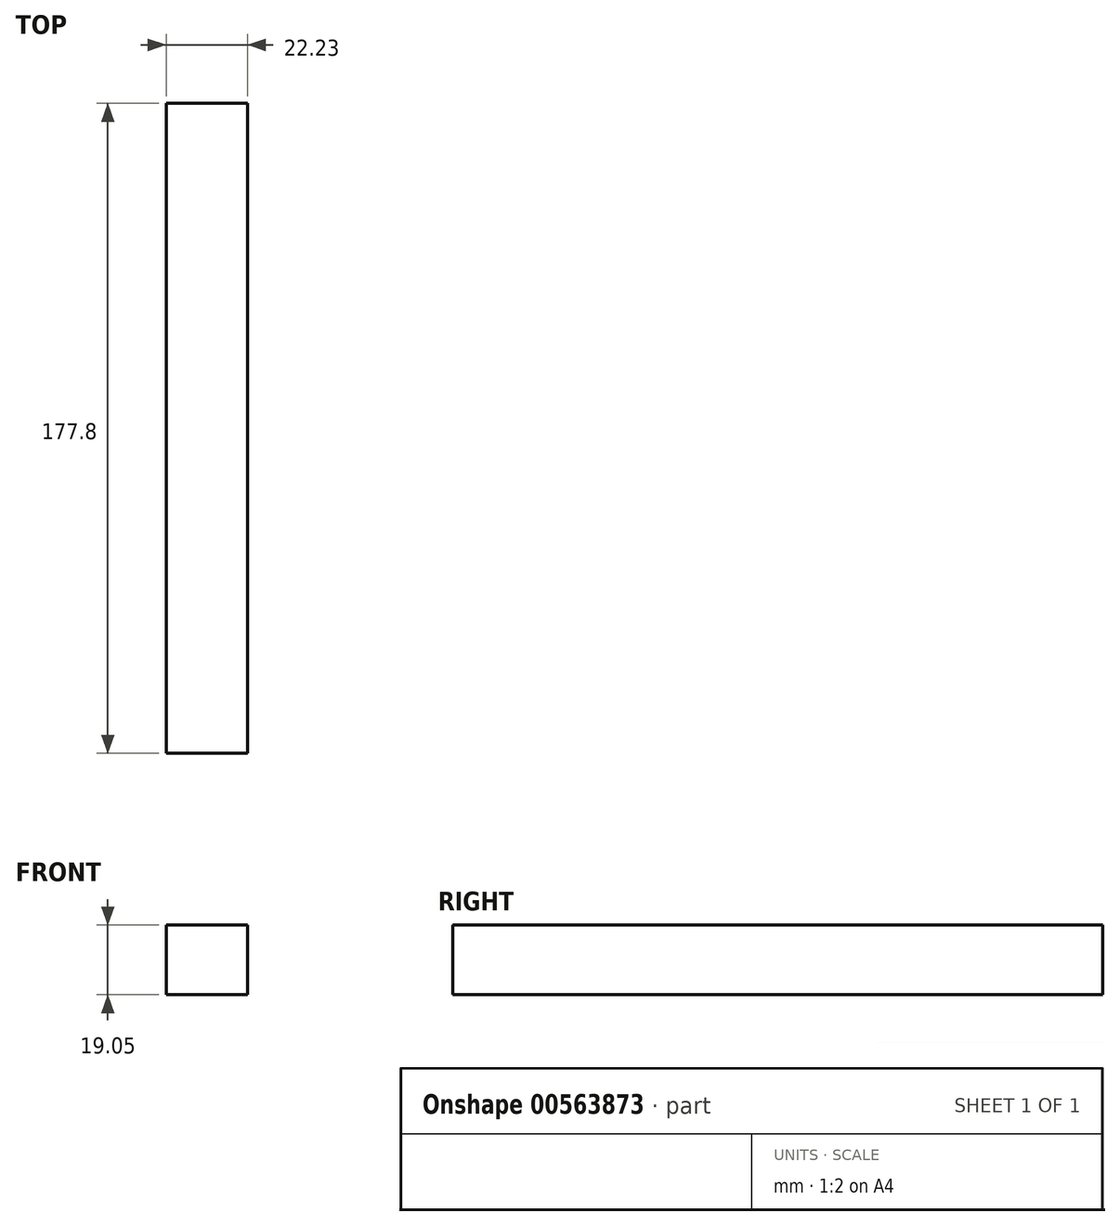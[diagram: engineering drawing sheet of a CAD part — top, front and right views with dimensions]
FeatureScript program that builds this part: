
annotation { "Feature Type Name" : "Feature", "Feature Type Description" : "" }
export const myFeature = defineFeature(function(context is Context, id is Id, definition is map)
    precondition{}
    {
        {
            var Q0;
            Q0=qCreatedBy(makeId("Front.planeOp"),FACE);
            var sketch = newSketch(context, id + "F0", { "sketchPlane" : qUnion([Q0])});
            skLineSegment(sketch, "E0.bottom", {"start": v(0, 0) * mm, "end": v(22.23, 0) * mm});
            skLineSegment(sketch, "E0.top", {"start": v(0, 19.05) * mm, "end": v(22.22, 19.05) * mm});
            skLineSegment(sketch, "E0.left", {"start": v(0, 0) * mm, "end": v(0, 19.05) * mm});
            skLineSegment(sketch, "E0.right", {"start": v(22.23, 0) * mm, "end": v(22.22, 19.05) * mm});
            skSolve(sketch);
        }
        {
            var Q0;
            Q0=makeQuery(id+"F0.imprint","IMPRINT",FACE,{"disambiguationData":[TD([[makeQuery(id+"F0.imprint","IMPRINT",EDGE,{"derivedFrom":sQuery(id+"F0.wireOp",EDGE,"E0.bottom")}),1.0]])]});
            extrude(context, id + "F1", {"entities" : qUnion([Q0]), "depth" : 177.8 * mm, "offsetDistance" : 25.4 * mm});
        }
    });
